# Revit family: Privacy-Screen_Scranton_WallHung
name_source: partatom
category: Casework
units: mm (PartAtom-declared; Revit-internal decimal feet)

## family parameters
Always vertical = Yes
Classification Number = 23.25.40.14.14.11
Cut with Voids When Loaded = No
Host = Wall
Room Calculation Point = No
Shared = No

## types (1)
- As Specified
    Assembly Code = C1010400
    Brackets_Vertical = 2
    Construction Details = http://www.arcat.com
    Default Elevation = 0' - 0"
    Description = Scranton Products Wall Mounted Privacy Screen
    Expected Lifespan (Years) = 0
    Green Building-LEED = http://www.arcat.com
    Hardware Finish = Chrome Plated Zamac
    Keynote = 10 21 00
    Maintenance Schedule (Months) = 0
    Manufacturer = Scranton Products
    Manufacturer Fax = 800-551-6993
    Manufacturer Website = http://www.scrantonproducts.com
    Manufacturer's Notes = Contact Manufacturer for More Information
    Material = Solid Plastic - Finish as Specified
    Model = Wall Hung Privacy Screen
    Panel Thickness = 0' - 0 7/8"
    Product Data = http://www.arcat.com
    Product Properties = http://www.scrantonproducts.com
    Reveal Clearance = 0' - 0 1/2"
    Revision = R1_03-2011
    Sales Information = http://www.scrantonproducts.com
    Send Message = http://www.arcat.com
    SpecWizard = http://www.arcat.com
    Specification = http://www.arcat.com
    Stall Width = 2' - 0"
    Test Data = http://www.scrantonproducts.com
    Type Comments = Privacy Screen
    URL = http://www.scrantonproducts.com
    Warranty Duration (Years) = 0

## geometry (parser evidence)
native form markers: Blend x66, Sweep x3
no freeform markers — native parametric forms only
